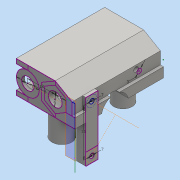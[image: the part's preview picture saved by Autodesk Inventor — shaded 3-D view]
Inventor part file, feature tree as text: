
AUTODESK INVENTOR PART (.ipt)
format: ipt  version: 2016 (Build 200138000, 138)  size: 244,224 bytes
history: native  units: mm
features: extrude x9, sketch x6, plane x1
ambient origin geometry x8: Origin, YZ Plane, XZ Plane, XY Plane, X Axis, Y Axis, Z Axis, Center Point
bodies: Solid1 (feature_tree)
feature tree (16):
  sketch  "Sketch1"  dims[d0=3.0mm d1=3.0mm]
  extrude  "Extrusion1"  Depth=3.0mm
  plane  "Work Plane6"
  sketch  "Sketch2"  dims[d3=31.0mm d6=7.0mm]
  extrude  "Extrusion6"  Depth=7.0mm
  extrude  "Extrusion5"  Depth=6.0mm TaperAngle=0.0deg
  sketch  "Sketch6"  dims[d7=7.0mm d9=6.0mm d10=0.0mm]
  extrude  "Extrusion8"  Depth=18.0mm
  extrude  "Extrusion9"  Depth=9.0mm
  extrude  "Extrusion10"  Depth=2.0mm TaperAngle=0.0deg
  extrude  "Extrusion11"  Depth=5.0mm TaperAngle=0.0deg
  extrude  "Extrusion12"  Depth=2.0mm
  extrude  "Extrusion13"  Depth=2.0mm
  sketch  "Sketch9"  dims[d26=-15.0mm d27=58.0mm d28=0.0mm d29=5.0mm d30=0.0mm d51=18.0mm d52=20.0mm d53=20.0mm d54=8.0mm d55=8.0mm d56=15.0mm d57=0.0mm d58=15.0mm d59=0.0mm d60=2.068392mm d61=2.52468mm d62=15.0mm d63=0.0mm d64=3.0mm d65=15.0mm d66=0.0mm d67=15.0mm d68=2.0mm d69=0.0mm d70=8.0mm d71=2.0mm d72=0.0mm]
  sketch  "Sketch7"  dims[d11=7.0mm d12=18.0mm]
  sketch  "Sketch8"  dims[d13=15.0mm d16=9.0mm]
